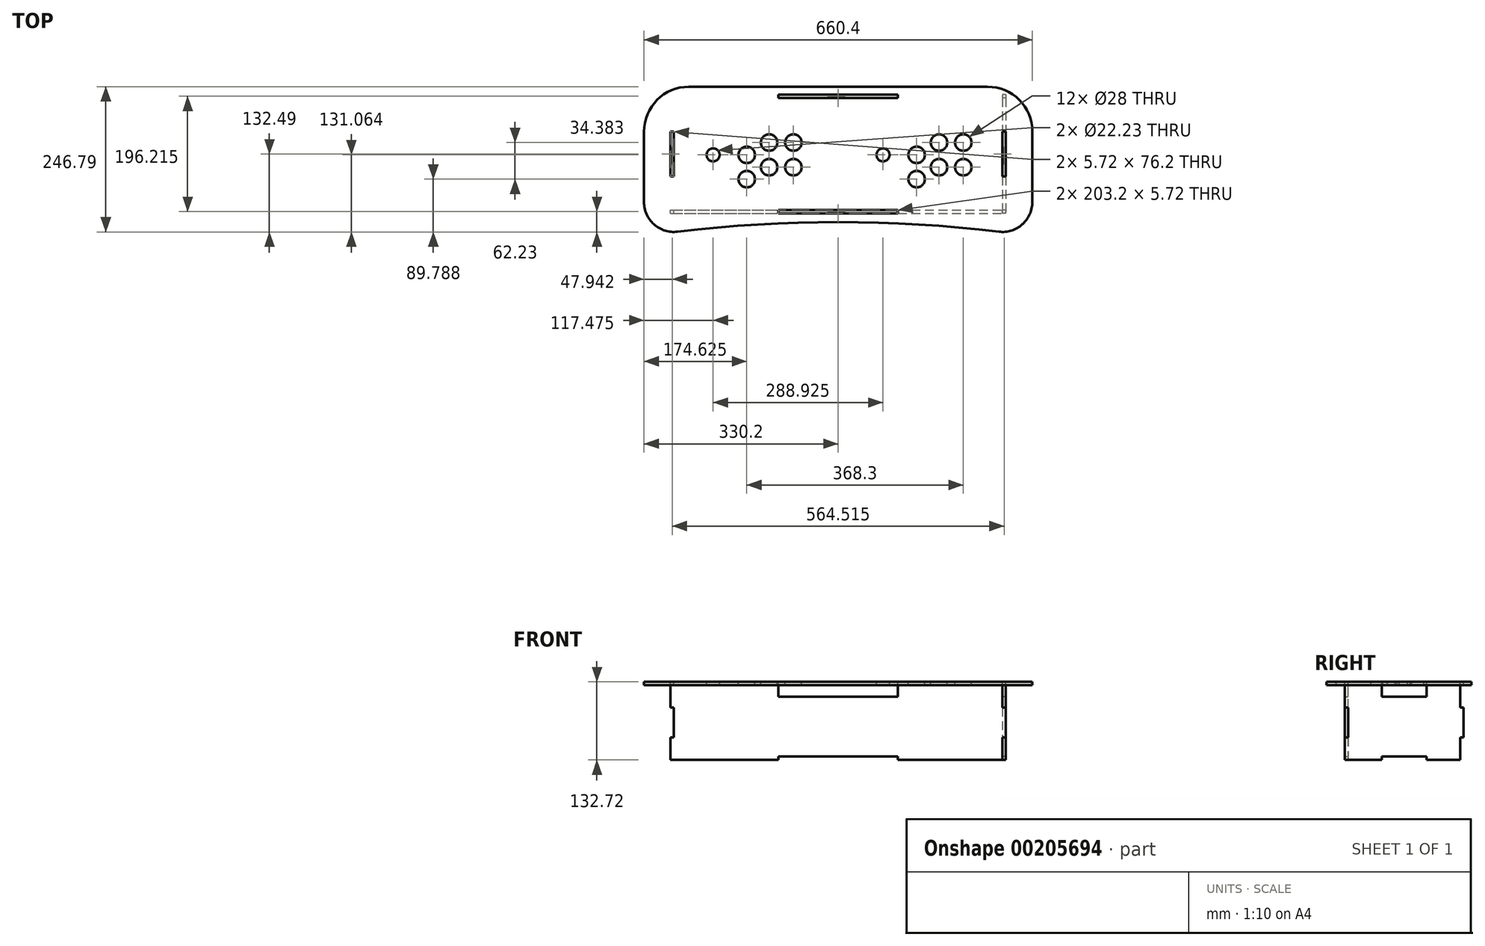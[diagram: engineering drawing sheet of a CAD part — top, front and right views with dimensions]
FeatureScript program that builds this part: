
annotation { "Feature Type Name" : "Feature", "Feature Type Description" : "" }
export const myFeature = defineFeature(function(context is Context, id is Id, definition is map)
    precondition{}
    {
        {
            var Q0;
            Q0=qCreatedBy(makeId("Top.planeOp"),FACE);
            var sketch = newSketch(context, id + "F0", { "sketchPlane" : qUnion([Q0])});
            skLineSegment(sketch, "E0.bottom", {"start": v(330.2, -127) * mm, "end": v(-330.2, -127) * mm});
            skLineSegment(sketch, "E0.top", {"start": v(330.2, 127) * mm, "end": v(-330.2, 127) * mm});
            skLineSegment(sketch, "E0.left", {"start": v(330.2, -127) * mm, "end": v(330.2, 127) * mm});
            skLineSegment(sketch, "E0.right", {"start": v(-330.2, -127) * mm, "end": v(-330.2, 127) * mm});
            skPoint(sketch, "E0.middle", {"position": v(0, 0) * mm});
            skSolve(sketch);
        }
        {
            var Q0;
            Q0=makeQuery(id+"F0.imprint","IMPRINT",FACE,{"disambiguationData":[TD([[makeQuery(id+"F0.imprint","IMPRINT",EDGE,{"derivedFrom":sQuery(id+"F0.wireOp",EDGE,"E0.bottom")}),-1.0]])]});
            extrude(context, id + "F1", {"entities" : qUnion([Q0]), "depth" : 5.7 * mm});
        }
        {
            var Q0;
            Q0=makeQuery(id+"F1.opExtrude","CAP_FACE",FACE,{"disambiguationData":[OSD([sQuery(id+"F0.wireOp",EDGE,"E0.bottom"),sQuery(id+"F0.wireOp",EDGE,"E0.top"),sQuery(id+"F0.wireOp",EDGE,"E0.left"),sQuery(id+"F0.wireOp",EDGE,"E0.right")])],"isStart":false});
            var sketch = newSketch(context, id + "F2", { "sketchPlane" : qUnion([Q0])});
            skArc(sketch, "E1", {"start": v(330.2, -127) * mm, "mid": v(0, -103.03) * mm, "end": v(-330.2, -127) * mm});
            skLineSegment(sketch, "E2", {"start": v(0, 127) * mm, "end": v(0, -127) * mm, "construction": true});
            skSolve(sketch);
        }
        {
            var Q0;
            {var subQ0=sQuery(id+"F2.wireOp",EDGE,"E1");Q0=makeQuery(id+"F2.imprint","IMPRINT",FACE,{"disambiguationData":[TD([[makeQuery(id+"F2.imprint","IMPRINT",EDGE,{"derivedFrom":subQ0}),1.0]])]});}
            extrude(context, id + "F3", {"entities" : qUnion([Q0]), "operationType" : NewBodyOperationType.REMOVE, "endBound" : BoundingType.THROUGH_ALL, "oppositeDirection" : true, "depth" : 25.4 * mm});
        }
        {
            var Q0;
            Q0=makeQuery(id+"F1.opExtrude","CAP_FACE",FACE,{"disambiguationData":[OSD([sQuery(id+"F0.wireOp",EDGE,"E0.bottom"),sQuery(id+"F0.wireOp",EDGE,"E0.top"),sQuery(id+"F0.wireOp",EDGE,"E0.left"),sQuery(id+"F0.wireOp",EDGE,"E0.right")])],"isStart":false});
            var sketch = newSketch(context, id + "F4", { "sketchPlane" : qUnion([Q0])});
            skSolve(sketch);
        }
        {
            var Q0;
            {var subQ0=sQuery(id+"F0.wireOp",EDGE,"E0.right");var subQ1=sQuery(id+"F0.wireOp",EDGE,"E0.bottom");Q0=makeQuery(id+"FBOf2KqEddd7jP7_1.boolean.opBoolean","MERGE",EDGE,{"derivedFrom":[makeQuery(id+"F1.opExtrude","SWEPT_EDGE",EDGE,{"disambiguationData":[OSD([subQ1,subQ0])]}),makeQuery(id+"FBOf2KqEddd7jP7_1.opExtrude","SWEPT_EDGE",EDGE,{"disambiguationData":[OSD([subQ1,subQ0,sQuery(id+"F4.wireOp",EDGE,"YZ262kwM-f9xy-yrOD-mAyZ-rjdBJHlWvZyA")])]})]});}
            var Q1;
            {var subQ0=sQuery(id+"F0.wireOp",EDGE,"E0.left");var subQ1=sQuery(id+"F0.wireOp",EDGE,"E0.bottom");Q1=makeQuery(id+"FBOf2KqEddd7jP7_1.boolean.opBoolean","MERGE",EDGE,{"derivedFrom":[makeQuery(id+"F1.opExtrude","SWEPT_EDGE",EDGE,{"disambiguationData":[OSD([subQ1,subQ0])]}),makeQuery(id+"FBOf2KqEddd7jP7_1.opExtrude","SWEPT_EDGE",EDGE,{"disambiguationData":[OSD([subQ1,subQ0,sQuery(id+"F4.wireOp",EDGE,"KTYkIo5P-So6Z-gEbL-5U7e-RvLePTOP2mm6")])]})]});}
            fillet(context, id + "F5", {"entities" : qUnion([Q0, Q1]), "radius" : 50.8 * mm, "tangentPropagation" : true, "allowEdgeOverflow" : false});
        }
        {
            var Q0;
            {var subQ0=sQuery(id+"F0.wireOp",EDGE,"E0.left");var subQ1=sQuery(id+"F0.wireOp",EDGE,"E0.right");Q0=makeQuery(id+"FBOf2KqEddd7jP7_1.boolean.opBoolean","MERGE",FACE,{"derivedFrom":[makeQuery(id+"F1.opExtrude","CAP_FACE",FACE,{"disambiguationData":[OSD([sQuery(id+"F0.wireOp",EDGE,"E0.bottom"),sQuery(id+"F0.wireOp",EDGE,"E0.top"),subQ0,subQ1])],"isStart":false}),makeQuery(id+"FBOf2KqEddd7jP7_1.opExtrude","CAP_FACE",FACE,{"disambiguationData":[OSD([subQ1,sQuery(id+"F4.wireOp",EDGE,"YZ262kwM-f9xy-yrOD-mAyZ-rjdBJHlWvZyA")])],"isStart":true}),makeQuery(id+"FBOf2KqEddd7jP7_1.opExtrude","CAP_FACE",FACE,{"disambiguationData":[OSD([subQ0,sQuery(id+"F4.wireOp",EDGE,"KTYkIo5P-So6Z-gEbL-5U7e-RvLePTOP2mm6")])],"isStart":true})]});}
            var sketch = newSketch(context, id + "F6", { "sketchPlane" : qUnion([Q0])});
            skLineSegment(sketch, "E3", {"start": v(0, 127) * mm, "end": v(0, -103.03) * mm, "construction": true});
            skLineSegment(sketch, "E4", {"start": v(-228.6, 11.27) * mm, "end": v(228.6, 11.27) * mm, "construction": true});
            skLineSegment(sketch, "E5", {"start": v(-212.73, 127) * mm, "end": v(-212.72, -112.95) * mm, "construction": true});
            skLineSegment(sketch, "E6", {"start": v(-117.48, 127) * mm, "end": v(-117.47, -106.05) * mm, "construction": true});
            skLineSegment(sketch, "E7", {"start": v(76.2, 127) * mm, "end": v(76.2, -104.3) * mm, "construction": true});
            skLineSegment(sketch, "E8", {"start": v(171.45, 127) * mm, "end": v(171.45, -109.46) * mm, "construction": true});
            skCircle(sketch, "E9", {"center": v(-212.72, 11.27) * mm, "radius": 11.11 * mm});
            skCircle(sketch, "E10", {"center": v(76.2, 11.27) * mm, "radius": 11.11 * mm});
            skCircle(sketch, "E11", {"center": v(-117.48, 32.23) * mm, "radius": 14 * mm});
            skCircle(sketch, "E12", {"center": v(-117.48, -9.68) * mm, "radius": 14 * mm});
            skCircle(sketch, "E13", {"center": v(-155.58, 11.27) * mm, "radius": 14 * mm});
            skCircle(sketch, "E14", {"center": v(-155.58, -30) * mm, "radius": 14 * mm});
            skCircle(sketch, "E15", {"center": v(-76.2, -9.68) * mm, "radius": 14 * mm});
            skCircle(sketch, "E16", {"center": v(-76.2, 32.23) * mm, "radius": 14 * mm});
            skCircle(sketch, "E17", {"center": v(171.45, 32.23) * mm, "radius": 14 * mm});
            skCircle(sketch, "E18", {"center": v(212.73, 32.23) * mm, "radius": 14 * mm});
            skCircle(sketch, "E19", {"center": v(212.73, -9.68) * mm, "radius": 14 * mm});
            skCircle(sketch, "E20", {"center": v(171.45, -9.68) * mm, "radius": 14 * mm});
            skCircle(sketch, "E21", {"center": v(133.35, 11.27) * mm, "radius": 14 * mm});
            skCircle(sketch, "E22", {"center": v(133.35, -30) * mm, "radius": 14 * mm});
            skLineSegment(sketch, "E23", {"start": v(-76.2, 32.23) * mm, "end": v(-76.2, -9.68) * mm, "construction": true});
            skSolve(sketch);
        }
        {
            var Q0;
            Q0 = qSketchRegion(id + "F6", true);
            extrude(context, id + "F7", {"entities" : qUnion([Q0]), "operationType" : NewBodyOperationType.REMOVE, "endBound" : BoundingType.THROUGH_ALL, "oppositeDirection" : true, "depth" : 25.4 * mm});
        }
        {
            var Q0;
            Q0=makeQuery(id+"F1.opExtrude","SWEPT_EDGE",EDGE,{"disambiguationData":[OSD([sQuery(id+"F0.wireOp",EDGE,"E0.top"),sQuery(id+"F0.wireOp",EDGE,"E0.right")])]});
            var Q1;
            Q1=makeQuery(id+"F1.opExtrude","SWEPT_EDGE",EDGE,{"disambiguationData":[OSD([sQuery(id+"F0.wireOp",EDGE,"E0.top"),sQuery(id+"F0.wireOp",EDGE,"E0.left")])]});
            fillet(context, id + "F8", {"entities" : qUnion([Q0, Q1]), "radius" : 76.2 * mm, "tangentPropagation" : true, "allowEdgeOverflow" : false});
        }
        {
            var Q0;
            Q0=makeQuery(id+"F4.imprint","IMPRINT",FACE,{"disambiguationData":[TD([[makeQuery(id+"F4.imprint","IMPRINT",EDGE,{"derivedFrom":makeQuery(id+"F1.opExtrude","CAP_EDGE",EDGE,{"disambiguationData":[OSD([sQuery(id+"F0.wireOp",EDGE,"E0.top")])],"isStart":false})}),1.0]])]});
            var sketch = newSketch(context, id + "F9", { "sketchPlane" : qUnion([Q0])});
            skLineSegment(sketch, "E24.bottom", {"start": v(-279.4, -82.55) * mm, "end": v(279.4, -82.55) * mm, "construction": true});
            skLineSegment(sketch, "E24.top", {"start": v(-279.4, 107.95) * mm, "end": v(279.4, 107.95) * mm, "construction": true});
            skLineSegment(sketch, "E24.left", {"start": v(-279.4, -82.55) * mm, "end": v(-279.4, 107.95) * mm, "construction": true});
            skLineSegment(sketch, "E24.right", {"start": v(279.4, -82.55) * mm, "end": v(279.4, 107.95) * mm, "construction": true});
            skPoint(sketch, "E24.middle", {"position": v(0, 12.7) * mm});
            skSolve(sketch);
        }
        {
            var Q0;
            Q0=qCreatedBy(makeId("Front.planeOp"),FACE);
            cPlane(context, id + "F10", {"entities" : qUnion([Q0]), "cplaneType" : CPlaneType.OFFSET, "offset" : 82.55 * mm, "width" : 152.4 * mm, "height" : 152.4 * mm});
        }
        {
            var Q0;
            Q0=qCreatedBy(id+"F10.planeOp",FACE);
            var sketch = newSketch(context, id + "F11", { "sketchPlane" : qUnion([Q0])});
            skLineSegment(sketch, "E25.bottom", {"start": v(-279.4, -127) * mm, "end": v(-101.6, -127) * mm});
            skLineSegment(sketch, "E25.top", {"start": v(-279.4, 0) * mm, "end": v(-101.6, 0) * mm});
            skLineSegment(sketch, "E25.left", {"start": v(-279.4, -127) * mm, "end": v(-279.4, -88.9) * mm, "construction": true});
            skLineSegment(sketch, "E25.right", {"start": v(279.4, -127) * mm, "end": v(279.4, -88.9) * mm});
            skPoint(sketch, "E25.middle", {"position": v(0, -63.5) * mm});
            skLineSegment(sketch, "E26.bottom", {"start": v(285.12, -38.1) * mm, "end": v(279.4, -38.1) * mm});
            skLineSegment(sketch, "E26.top", {"start": v(285.12, -88.9) * mm, "end": v(279.4, -88.9) * mm});
            skLineSegment(sketch, "E26.left", {"start": v(285.11, -38.1) * mm, "end": v(285.11, -88.9) * mm});
            skPoint(sketch, "E26.middle", {"position": v(279.4, -63.5) * mm});
            skLineSegment(sketch, "E27.bottom", {"start": v(-273.69, -88.9) * mm, "end": v(-279.4, -88.9) * mm, "construction": true});
            skLineSegment(sketch, "E27.top", {"start": v(-273.69, -38.1) * mm, "end": v(-279.4, -38.1) * mm, "construction": true});
            skLineSegment(sketch, "E27.left", {"start": v(-273.69, -88.9) * mm, "end": v(-273.69, -38.1) * mm, "construction": true});
            skPoint(sketch, "E27.middle", {"position": v(-279.4, -63.5) * mm});
            skLineSegment(sketch, "E28.trimOffspring", {"start": v(-279.4, -38.1) * mm, "end": v(-279.4, 0) * mm, "construction": true});
            skLineSegment(sketch, "E29.trimOffspring", {"start": v(279.4, -38.1) * mm, "end": v(279.4, 0) * mm});
            skPoint(sketch, "E26.right.start.orphan", {"position": v(273.68, -38.1) * mm});
            skPoint(sketch, "E30.orphan", {"position": v(273.69, -88.9) * mm});
            skLineSegment(sketch, "E31.top", {"start": v(101.6, -121.28) * mm, "end": v(-101.6, -121.28) * mm});
            skLineSegment(sketch, "E31.left", {"start": v(101.6, -127) * mm, "end": v(101.6, -121.28) * mm});
            skLineSegment(sketch, "E31.right", {"start": v(-101.6, -127) * mm, "end": v(-101.6, -121.28) * mm});
            skPoint(sketch, "E31.middle", {"position": v(0, -127) * mm});
            skLineSegment(sketch, "E32.trimOffspring", {"start": v(101.6, -127) * mm, "end": v(279.4, -127) * mm});
            skPoint(sketch, "E33.orphan", {"position": v(101.6, -132.71) * mm});
            skPoint(sketch, "E34.orphan", {"position": v(-101.6, -132.71) * mm});
            skLineSegment(sketch, "E35.top", {"start": v(101.6, 5.72) * mm, "end": v(-101.6, 5.72) * mm});
            skLineSegment(sketch, "E35.left", {"start": v(101.6, 0) * mm, "end": v(101.6, 5.72) * mm});
            skLineSegment(sketch, "E35.right", {"start": v(-101.6, 0) * mm, "end": v(-101.6, 5.72) * mm});
            skPoint(sketch, "E35.middle", {"position": v(0, 0) * mm});
            skLineSegment(sketch, "E36.trimOffspring", {"start": v(101.6, 0) * mm, "end": v(279.4, 0) * mm});
            skPoint(sketch, "E37.orphan", {"position": v(101.6, -5.72) * mm});
            skPoint(sketch, "E38.orphan", {"position": v(-101.6, -5.72) * mm});
            skLineSegment(sketch, "E39", {"start": v(-285.12, 0) * mm, "end": v(-285.12, -38.1) * mm});
            skLineSegment(sketch, "E40", {"start": v(-285.12, -38.1) * mm, "end": v(-279.4, -38.1) * mm});
            skLineSegment(sketch, "E41", {"start": v(-279.4, -38.1) * mm, "end": v(-279.4, -88.9) * mm});
            skLineSegment(sketch, "E42", {"start": v(-279.4, -88.9) * mm, "end": v(-285.12, -88.9) * mm});
            skLineSegment(sketch, "E43", {"start": v(-285.12, -88.9) * mm, "end": v(-285.12, -127) * mm});
            skLineSegment(sketch, "E44", {"start": v(-285.12, 0) * mm, "end": v(-279.4, 0) * mm});
            skLineSegment(sketch, "E45", {"start": v(-285.12, -127) * mm, "end": v(-279.4, -127) * mm});
            skSolve(sketch);
        }
        {
            var Q0;
            Q0 = qSketchRegion(id + "F11", true);
            extrude(context, id + "F12", {"entities" : qUnion([Q0]), "depth" : 5.7 * mm});
        }
        {
            var Q0;
            Q0=qCreatedBy(makeId("Right.planeOp"),FACE);
            cPlane(context, id + "F13", {"entities" : qUnion([Q0]), "cplaneType" : CPlaneType.OFFSET, "offset" : 279.4 * mm, "width" : 152.4 * mm, "height" : 152.4 * mm});
        }
        {
            var Q0;
            Q0=qCreatedBy(id+"F13.planeOp",FACE);
            var sketch = newSketch(context, id + "F14", { "sketchPlane" : qUnion([Q0])});
            skLineSegment(sketch, "E46", {"start": v(12.7, 5.71) * mm, "end": v(12.7, -333.33) * mm, "construction": true});
            skLineSegment(sketch, "E47.bottom", {"start": v(107.95, -127) * mm, "end": v(50.8, -127) * mm});
            skLineSegment(sketch, "E47.top", {"start": v(107.95, 0) * mm, "end": v(-82.55, 0) * mm});
            skPoint(sketch, "E47.middle", {"position": v(12.7, -63.5) * mm});
            skLineSegment(sketch, "E48", {"start": v(-82.55, -127) * mm, "end": v(-82.55, -88.9) * mm});
            skLineSegment(sketch, "E49", {"start": v(-82.55, -88.9) * mm, "end": v(-88.27, -88.9) * mm});
            skLineSegment(sketch, "E50", {"start": v(-88.27, -38.1) * mm, "end": v(-82.55, -38.1) * mm});
            skLineSegment(sketch, "E51", {"start": v(-82.55, -38.1) * mm, "end": v(-82.55, 0) * mm});
            skPoint(sketch, "E52.orphan", {"position": v(-88.27, 0) * mm});
            skLineSegment(sketch, "E53.top", {"start": v(50.8, -121.29) * mm, "end": v(-25.4, -121.29) * mm});
            skLineSegment(sketch, "E53.left", {"start": v(50.8, -127) * mm, "end": v(50.8, -121.29) * mm});
            skLineSegment(sketch, "E53.right", {"start": v(-25.4, -127) * mm, "end": v(-25.4, -121.29) * mm});
            skPoint(sketch, "E53.middle", {"position": v(12.7, -127) * mm});
            skLineSegment(sketch, "E54.trimOffspring", {"start": v(-25.4, -127) * mm, "end": v(-82.55, -127) * mm});
            skPoint(sketch, "E53.bottom.end.orphan", {"position": v(-25.4, -132.71) * mm});
            skPoint(sketch, "E55.orphan", {"position": v(50.8, -132.71) * mm});
            skLineSegment(sketch, "E56", {"start": v(-88.27, -38.1) * mm, "end": v(-88.27, 28.47) * mm});
            skLineSegment(sketch, "E57", {"start": v(-82.55, 0) * mm, "end": v(-102.92, 0) * mm});
            skLineSegment(sketch, "E58", {"start": v(-88.27, -88.9) * mm, "end": v(-88.27, -145.38) * mm});
            skLineSegment(sketch, "E59", {"start": v(-82.55, -127) * mm, "end": v(-111.14, -127) * mm});
            skLineSegment(sketch, "E60", {"start": v(-82.55, -38.1) * mm, "end": v(-82.55, -88.9) * mm});
            skLineSegment(sketch, "E61.top", {"start": v(50.8, 5.71) * mm, "end": v(-25.4, 5.71) * mm});
            skLineSegment(sketch, "E61.left", {"start": v(50.8, 0) * mm, "end": v(50.8, 5.71) * mm});
            skLineSegment(sketch, "E61.right", {"start": v(-25.4, 0) * mm, "end": v(-25.4, 5.71) * mm});
            skPoint(sketch, "E61.middle", {"position": v(12.7, 0) * mm});
            skPoint(sketch, "E62.orphan", {"position": v(-25.4, -5.72) * mm});
            skPoint(sketch, "E63.orphan", {"position": v(50.8, -5.72) * mm});
            skLineSegment(sketch, "E64", {"start": v(113.66, -38.1) * mm, "end": v(113.66, -88.9) * mm});
            skLineSegment(sketch, "E65", {"start": v(107.95, 0) * mm, "end": v(107.95, -38.1) * mm});
            skLineSegment(sketch, "E66", {"start": v(107.95, -38.1) * mm, "end": v(113.66, -38.1) * mm});
            skLineSegment(sketch, "E67", {"start": v(113.67, -88.9) * mm, "end": v(107.95, -88.9) * mm});
            skLineSegment(sketch, "E68", {"start": v(107.95, -88.9) * mm, "end": v(107.95, -127) * mm});
            skPoint(sketch, "E69.orphan", {"position": v(113.67, -127) * mm});
            skPoint(sketch, "E70.orphan", {"position": v(113.66, 0) * mm});
            skSolve(sketch);
        }
        {
            var Q0;
            Q0 = qSketchRegion(id + "F14", true);
            extrude(context, id + "F15", {"entities" : qUnion([Q0]), "depth" : 5.7 * mm});
        }
        {
            var Q0;
            Q0=makeQuery(id+"F9.imprint","IMPRINT",FACE,{"disambiguationData":[TD([[makeQuery(id+"F9.imprint","IMPRINT",EDGE,{"derivedFrom":makeQuery(id+"F4.imprint","IMPRINT",EDGE,{"derivedFrom":makeQuery(id+"F1.opExtrude","CAP_EDGE",EDGE,{"disambiguationData":[OSD([sQuery(id+"F0.wireOp",EDGE,"E0.top")])],"isStart":false})})}),1.0]])]});
            var sketch = newSketch(context, id + "F16", { "sketchPlane" : qUnion([Q0])});
            skLineSegment(sketch, "E71.bottom", {"start": v(-282.26, -85.4) * mm, "end": v(282.26, -85.4) * mm, "construction": true});
            skLineSegment(sketch, "E71.top", {"start": v(-282.26, 110.8) * mm, "end": v(282.26, 110.8) * mm, "construction": true});
            skLineSegment(sketch, "E71.left", {"start": v(-282.26, -85.4) * mm, "end": v(-282.26, 110.8) * mm, "construction": true});
            skLineSegment(sketch, "E71.right", {"start": v(282.26, -85.4) * mm, "end": v(282.26, 110.8) * mm, "construction": true});
            skPoint(sketch, "E71.middle", {"position": v(0, 12.7) * mm});
            skLineSegment(sketch, "E72.bottom", {"start": v(101.6, -88.27) * mm, "end": v(-101.6, -88.26) * mm});
            skLineSegment(sketch, "E72.top", {"start": v(101.6, -82.55) * mm, "end": v(-101.6, -82.55) * mm});
            skLineSegment(sketch, "E72.left", {"start": v(101.6, -88.27) * mm, "end": v(101.6, -82.55) * mm});
            skLineSegment(sketch, "E72.right", {"start": v(-101.6, -88.27) * mm, "end": v(-101.6, -82.55) * mm});
            skPoint(sketch, "E72.middle", {"position": v(0, -85.4) * mm});
            skLineSegment(sketch, "E73.bottom", {"start": v(101.6, 107.95) * mm, "end": v(-101.6, 107.95) * mm});
            skLineSegment(sketch, "E73.top", {"start": v(101.6, 113.67) * mm, "end": v(-101.6, 113.67) * mm});
            skLineSegment(sketch, "E73.left", {"start": v(101.6, 107.95) * mm, "end": v(101.6, 113.67) * mm});
            skLineSegment(sketch, "E73.right", {"start": v(-101.6, 107.95) * mm, "end": v(-101.6, 113.67) * mm});
            skPoint(sketch, "E73.middle", {"position": v(0, 110.8) * mm});
            skLineSegment(sketch, "E74.bottom", {"start": v(285.12, -25.4) * mm, "end": v(279.4, -25.4) * mm});
            skLineSegment(sketch, "E74.top", {"start": v(285.12, 50.8) * mm, "end": v(279.4, 50.8) * mm});
            skLineSegment(sketch, "E74.left", {"start": v(285.12, -25.4) * mm, "end": v(285.12, 50.8) * mm});
            skLineSegment(sketch, "E74.right", {"start": v(279.4, -25.4) * mm, "end": v(279.4, 50.8) * mm});
            skPoint(sketch, "E74.middle", {"position": v(282.26, 12.7) * mm});
            skLineSegment(sketch, "E75.bottom", {"start": v(-279.4, -25.4) * mm, "end": v(-285.12, -25.4) * mm});
            skLineSegment(sketch, "E75.top", {"start": v(-279.4, 50.8) * mm, "end": v(-285.12, 50.8) * mm});
            skLineSegment(sketch, "E75.left", {"start": v(-279.4, -25.4) * mm, "end": v(-279.4, 50.8) * mm});
            skLineSegment(sketch, "E75.right", {"start": v(-285.12, -25.4) * mm, "end": v(-285.12, 50.8) * mm});
            skPoint(sketch, "E75.middle", {"position": v(-282.26, 12.7) * mm});
            skSolve(sketch);
        }
        {
            var Q0;
            Q0 = qSketchRegion(id + "F16", true);
            extrude(context, id + "F17", {"entities" : qUnion([Q0]), "operationType" : NewBodyOperationType.REMOVE, "oppositeDirection" : true, "depth" : 25.4 * mm});
        }
        {
            var Q0;
            Q0=makeQuery(id+"F1.opExtrude","CAP_FACE",FACE,{"disambiguationData":[OSD([sQuery(id+"F0.wireOp",EDGE,"E0.bottom"),sQuery(id+"F0.wireOp",EDGE,"E0.top"),sQuery(id+"F0.wireOp",EDGE,"E0.left"),sQuery(id+"F0.wireOp",EDGE,"E0.right")])],"isStart":true});
            cPlane(context, id + "F18", {"entities" : qUnion([Q0]), "cplaneType" : CPlaneType.OFFSET, "offset" : 127 * mm, "width" : 152.4 * mm, "height" : 152.4 * mm});
        }
    });
